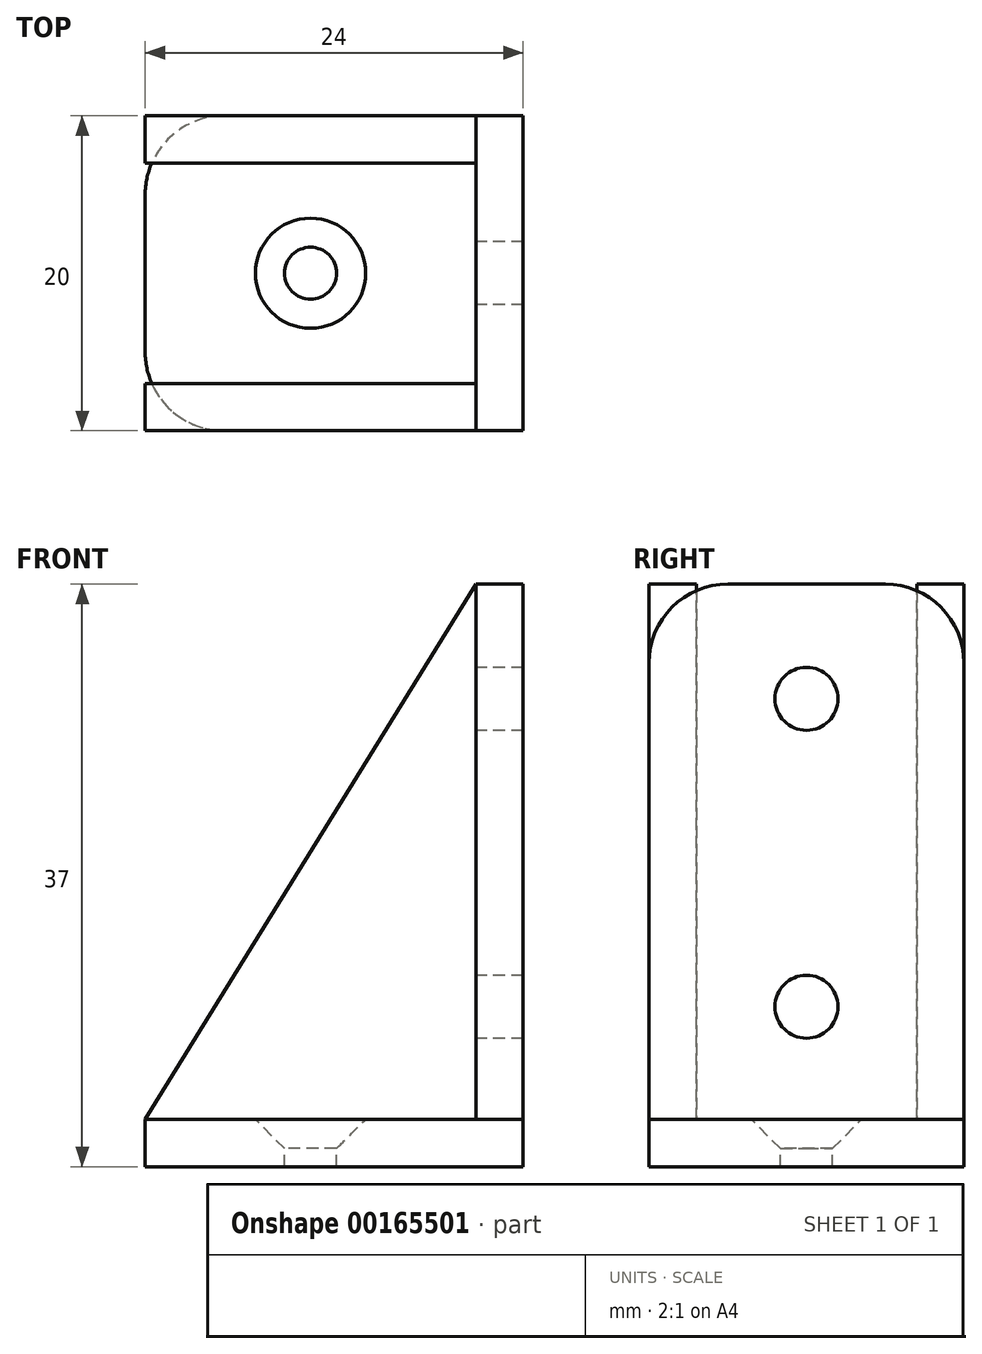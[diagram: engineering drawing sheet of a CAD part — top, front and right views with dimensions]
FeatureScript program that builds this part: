
annotation { "Feature Type Name" : "Feature", "Feature Type Description" : "" }
export const myFeature = defineFeature(function(context is Context, id is Id, definition is map)
    precondition{}
    {
        {
            var Q0;
            Q0=qCreatedBy(makeId("Top.planeOp"),FACE);
            var sketch = newSketch(context, id + "F0", { "sketchPlane" : qUnion([Q0])});
            skLineSegment(sketch, "E0", {"start": v(0, 0) * mm, "end": v(0, 10) * mm});
            skLineSegment(sketch, "E1", {"start": v(0, 10) * mm, "end": v(24, 10) * mm});
            skLineSegment(sketch, "E2", {"start": v(24, 10) * mm, "end": v(24, 0) * mm});
            skLineSegment(sketch, "E3.MirrorCS", {"start": v(0, 0) * mm, "end": v(0, -10) * mm});
            skLineSegment(sketch, "E4.MirrorCS", {"start": v(0, -10) * mm, "end": v(24, -10) * mm});
            skLineSegment(sketch, "E5.MirrorCS", {"start": v(24, -10) * mm, "end": v(24, 0) * mm});
            skSolve(sketch);
        }
        {
            var Q0;
            Q0 = qSketchRegion(id + "F0", true);
            extrude(context, id + "F1", {"entities" : qUnion([Q0]), "depth" : 3 * mm});
        }
        {
            var Q0;
            Q0=makeQuery(id+"F1.opExtrude","CAP_FACE",FACE,{"disambiguationData":[OSD([sQuery(id+"F0.wireOp",EDGE,"E0"),sQuery(id+"F0.wireOp",EDGE,"E1"),sQuery(id+"F0.wireOp",EDGE,"E2"),sQuery(id+"F0.wireOp",EDGE,"E3.MirrorCS"),sQuery(id+"F0.wireOp",EDGE,"E4.MirrorCS"),sQuery(id+"F0.wireOp",EDGE,"E5.MirrorCS")])],"isStart":false});
            var sketch = newSketch(context, id + "F2", { "sketchPlane" : qUnion([Q0])});
            skLineSegment(sketch, "E6.0", {"start": v(24, -10) * mm, "end": v(24, 10) * mm});
            skLineSegment(sketch, "E6.1", {"start": v(21, 10) * mm, "end": v(24, 10) * mm});
            skLineSegment(sketch, "E6.2", {"start": v(21, -10) * mm, "end": v(24, -10) * mm});
            skLineSegment(sketch, "E7", {"start": v(21, 10) * mm, "end": v(21, -10) * mm});
            skPoint(sketch, "E8.orphan", {"position": v(0, 10) * mm});
            skPoint(sketch, "E9.orphan", {"position": v(0, -10) * mm});
            skSolve(sketch);
        }
        {
            var Q0;
            Q0 = qSketchRegion(id + "F2", true);
            extrude(context, id + "F3", {"entities" : qUnion([Q0]), "depth" : 34 * mm});
        }
        {
            var Q0;
            Q0=makeQuery(id+"F1.opExtrude","SWEPT_FACE",FACE,{"disambiguationData":[OSD([sQuery(id+"F0.wireOp",EDGE,"E4.MirrorCS")])]});
            var sketch = newSketch(context, id + "F4", { "sketchPlane" : qUnion([Q0])});
            skLineSegment(sketch, "E10.0", {"start": v(21, 37) * mm, "end": v(21, 3) * mm});
            skLineSegment(sketch, "E10.1", {"start": v(0, 3) * mm, "end": v(21, 3) * mm});
            skLineSegment(sketch, "E11", {"start": v(0, 3) * mm, "end": v(21, 37) * mm});
            skPoint(sketch, "E12.orphan", {"position": v(24, 3) * mm});
            skSolve(sketch);
        }
        {
            var Q0;
            Q0 = qSketchRegion(id + "F4", true);
            extrude(context, id + "F5", {"entities" : qUnion([Q0]), "oppositeDirection" : true, "depth" : 3 * mm});
        }
        {
            var Q0;
            Q0=makeQuery(id+"F5.opExtrude","SWEPT_BODY",BODY,{"disambiguationData":[OSD([sQuery(id+"F4.wireOp",EDGE,"E10.0"),sQuery(id+"F4.wireOp",EDGE,"E10.1"),sQuery(id+"F4.wireOp",EDGE,"E11")])]});
            var Q1;
            Q1=qCreatedBy(makeId("Front.planeOp"),FACE);
            mirror(context, id + "F6", {"entities" : qUnion([Q0]), "mirrorPlane" : qUnion([Q1])});
        }
        {
            var Q0;
            Q0=makeQuery(id+"F3.opExtrude","SWEPT_FACE",FACE,{"disambiguationData":[OSD([sQuery(id+"F2.wireOp",EDGE,"E7")])]});
            var sketch = newSketch(context, id + "F7", { "sketchPlane" : qUnion([Q0])});
            skPoint(sketch, "E13", {"position": v(0, 10.16) * mm});
            skPoint(sketch, "E14", {"position": v(0, 29.72) * mm});
            skSolve(sketch);
        }
        {
            var Q0;
            Q0=sQuery(id+"F7.wireOp",VERTEX,"E13");
            var Q1;
            Q1=sQuery(id+"F7.wireOp",VERTEX,"E14");
            var Q2;
            Q2=makeQuery(id+"F3.opExtrude","SWEPT_BODY",BODY,{"disambiguationData":[OSD([sQuery(id+"F2.wireOp",EDGE,"E6.0"),sQuery(id+"F2.wireOp",EDGE,"E6.1"),sQuery(id+"F2.wireOp",EDGE,"E6.2"),sQuery(id+"F2.wireOp",EDGE,"E7")])]});
            hole(context, id + "F8", {"style" : HoleStyle.SIMPLE, "endStyle" : HoleEndStyle.THROUGH, "holeDiameter" : 4 * mm, "locations" : qUnion([Q0, Q1]), "scope" : qUnion([Q2]), "isTappedThrough" : true});
        }
        {
            var Q0;
            Q0=makeQuery(id+"F1.opExtrude","CAP_FACE",FACE,{"disambiguationData":[OSD([sQuery(id+"F0.wireOp",EDGE,"E0"),sQuery(id+"F0.wireOp",EDGE,"E1"),sQuery(id+"F0.wireOp",EDGE,"E2"),sQuery(id+"F0.wireOp",EDGE,"E3.MirrorCS"),sQuery(id+"F0.wireOp",EDGE,"E4.MirrorCS"),sQuery(id+"F0.wireOp",EDGE,"E5.MirrorCS")])],"isStart":false});
            var sketch = newSketch(context, id + "F9", { "sketchPlane" : qUnion([Q0])});
            skPoint(sketch, "E15", {"position": v(10.5, 0) * mm});
            skLineSegment(sketch, "E16.0", {"start": v(21, 10) * mm, "end": v(21, -10) * mm, "construction": true});
            skLineSegment(sketch, "E16.1", {"start": v(0, 7) * mm, "end": v(21, 7) * mm, "construction": true});
            skLineSegment(sketch, "E16.2", {"start": v(0, -10) * mm, "end": v(0, 10) * mm, "construction": true});
            skLineSegment(sketch, "E16.3", {"start": v(0, -7) * mm, "end": v(21, -7) * mm, "construction": true});
            skLineSegment(sketch, "E17", {"start": v(21, 7) * mm, "end": v(0, -7) * mm, "construction": true});
            skLineSegment(sketch, "E18", {"start": v(0, 7) * mm, "end": v(21, -7) * mm, "construction": true});
            skSolve(sketch);
        }
        {
            var Q0;
            Q0=sQuery(id+"F9.wireOp",VERTEX,"E15");
            var Q1;
            Q1=makeQuery(id+"F1.opExtrude","SWEPT_BODY",BODY,{"disambiguationData":[OSD([sQuery(id+"F0.wireOp",EDGE,"E0"),sQuery(id+"F0.wireOp",EDGE,"E1"),sQuery(id+"F0.wireOp",EDGE,"E2"),sQuery(id+"F0.wireOp",EDGE,"E3.MirrorCS"),sQuery(id+"F0.wireOp",EDGE,"E4.MirrorCS"),sQuery(id+"F0.wireOp",EDGE,"E5.MirrorCS")])]});
            hole(context, id + "F10", {"style" : HoleStyle.C_SINK, "endStyle" : HoleEndStyle.THROUGH, "holeDiameter" : 3.3 * mm, "cSinkDiameter" : 7 * mm, "cSinkAngle" : 90 * degree, "locations" : qUnion([Q0]), "scope" : qUnion([Q1]), "isTappedThrough" : true});
        }
        {
            var Q0;
            Q0=makeQuery(id+"F1.opExtrude","SWEPT_EDGE",EDGE,{"disambiguationData":[OSD([sQuery(id+"F0.wireOp",EDGE,"E3.MirrorCS"),sQuery(id+"F0.wireOp",EDGE,"E4.MirrorCS")])]});
            var Q1;
            Q1=makeQuery(id+"F1.opExtrude","SWEPT_EDGE",EDGE,{"disambiguationData":[OSD([sQuery(id+"F0.wireOp",EDGE,"E0"),sQuery(id+"F0.wireOp",EDGE,"E1")])]});
            var Q2;
            Q2=makeQuery(id+"F3.opExtrude","CAP_EDGE",EDGE,{"disambiguationData":[OSD([sQuery(id+"F2.wireOp",EDGE,"E6.2")])],"isStart":false});
            var Q3;
            Q3=makeQuery(id+"F3.opExtrude","CAP_EDGE",EDGE,{"disambiguationData":[OSD([sQuery(id+"F2.wireOp",EDGE,"E6.1")])],"isStart":false});
            fillet(context, id + "F11", {"entities" : qUnion([Q0, Q1, Q2, Q3]), "radius" : 5 * mm, "tangentPropagation" : true, "allowEdgeOverflow" : false});
        }
    });
